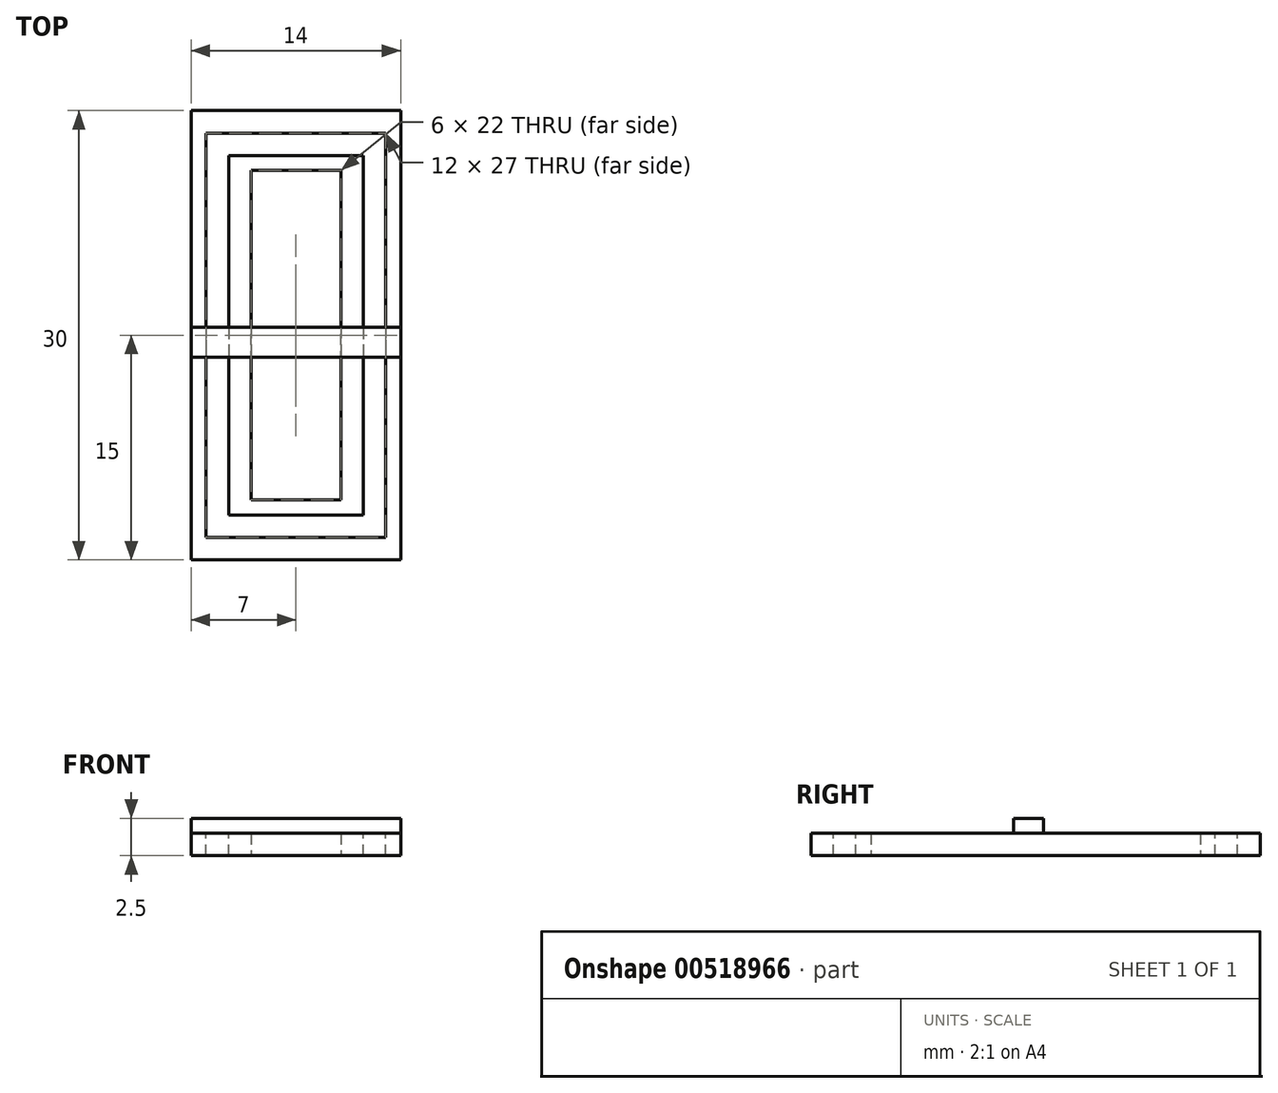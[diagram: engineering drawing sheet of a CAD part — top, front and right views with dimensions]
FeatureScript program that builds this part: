
annotation { "Feature Type Name" : "Feature", "Feature Type Description" : "" }
export const myFeature = defineFeature(function(context is Context, id is Id, definition is map)
    precondition{}
    {
        {
            var Q0;
            Q0=qCreatedBy(makeId("Top.planeOp"),FACE);
            var sketch = newSketch(context, id + "F0", { "sketchPlane" : qUnion([Q0])});
            skLineSegment(sketch, "E0.bottom", {"start": v(-3, 11) * mm, "end": v(3, 11) * mm});
            skLineSegment(sketch, "E0.top", {"start": v(-3, -11) * mm, "end": v(3, -11) * mm});
            skLineSegment(sketch, "E0.left", {"start": v(-3, 11) * mm, "end": v(-3, -11) * mm});
            skLineSegment(sketch, "E0.right", {"start": v(3, 11) * mm, "end": v(3, -11) * mm});
            skLineSegment(sketch, "E1.bottom", {"start": v(-7, 15) * mm, "end": v(7, 15) * mm});
            skLineSegment(sketch, "E1.top", {"start": v(-7, -15) * mm, "end": v(7, -15) * mm});
            skLineSegment(sketch, "E1.left", {"start": v(-7, 15) * mm, "end": v(-7, -15) * mm});
            skLineSegment(sketch, "E1.right", {"start": v(7, 15) * mm, "end": v(7, -15) * mm});
            skLineSegment(sketch, "E2", {"start": v(-3.5, 15) * mm, "end": v(-3.5, 11) * mm, "construction": true});
            skLineSegment(sketch, "E3", {"start": v(3, 0) * mm, "end": v(7, 0) * mm, "construction": true});
            skPoint(sketch, "E3.startSnap0", {"position": v(7, 0) * mm});
            skLineSegment(sketch, "E4", {"start": v(-3, -8.4) * mm, "end": v(-7, -8.4) * mm, "construction": true});
            skLineSegment(sketch, "E5", {"start": v(-2.31, -11) * mm, "end": v(-2.31, -15) * mm, "construction": true});
            skCircle(sketch, "E6", {"center": v(0, 0) * mm, "radius": 2.25 * mm});
            skLineSegment(sketch, "E7", {"start": v(0, 0) * mm, "end": v(0, -11) * mm, "construction": true});
            skLineSegment(sketch, "E8", {"start": v(0, 0) * mm, "end": v(3, 0) * mm, "construction": true});
            skSolve(sketch);
        }
        {
            var Q0;
            Q0=makeQuery(id+"F0.imprint","IMPRINT",FACE,{"disambiguationData":[TD([[makeQuery(id+"F0.imprint","IMPRINT",EDGE,{"derivedFrom":sQuery(id+"F0.wireOp",EDGE,"E0.bottom")}),1.0]])]});
            var Q1;
            Q1=makeQuery(id+"F0.imprint","IMPRINT",FACE,{"disambiguationData":[TD([[makeQuery(id+"F0.imprint","IMPRINT",EDGE,{"derivedFrom":sQuery(id+"F0.wireOp",EDGE,"E0.bottom")}),-1.0]])]});
            extrude(context, id + "F1", {"entities" : qUnion([Q0, Q1]), "oppositeDirection" : true, "depth" : 2.5 * mm, "offsetDistance" : 25 * mm});
        }
        {
            var Q0;
            Q0=makeQuery(id+"F0.imprint","IMPRINT",FACE,{"disambiguationData":[TD([[makeQuery(id+"F0.imprint","IMPRINT",EDGE,{"derivedFrom":sQuery(id+"F0.wireOp",EDGE,"E0.bottom")}),1.0]])]});
            extrude(context, id + "F2", {"entities" : qUnion([Q0]), "operationType" : NewBodyOperationType.ADD, "depth" : 5 * mm, "offsetDistance" : 25 * mm});
        }
        {
            var Q0;
            Q0=makeQuery(id+"F2.opExtrude","CAP_FACE",FACE,{"disambiguationData":[OSD([sQuery(id+"F0.wireOp",EDGE,"E0.bottom"),sQuery(id+"F0.wireOp",EDGE,"E0.top"),sQuery(id+"F0.wireOp",EDGE,"E0.left"),sQuery(id+"F0.wireOp",EDGE,"E0.right"),sQuery(id+"F0.wireOp",EDGE,"E1.bottom"),sQuery(id+"F0.wireOp",EDGE,"E1.top"),sQuery(id+"F0.wireOp",EDGE,"E1.left"),sQuery(id+"F0.wireOp",EDGE,"E1.right")])],"isStart":false});
            var sketch = newSketch(context, id + "F3", { "sketchPlane" : qUnion([Q0])});
            skLineSegment(sketch, "E9.bottom", {"start": v(-6, 13.5) * mm, "end": v(6, 13.5) * mm});
            skLineSegment(sketch, "E9.top", {"start": v(-6, -13.5) * mm, "end": v(6, -13.5) * mm});
            skLineSegment(sketch, "E9.left", {"start": v(-6, 13.5) * mm, "end": v(-6, -13.5) * mm});
            skLineSegment(sketch, "E9.right", {"start": v(6, 13.5) * mm, "end": v(6, -13.5) * mm});
            skLineSegment(sketch, "E10.bottom", {"start": v(-4.5, 12) * mm, "end": v(4.5, 12) * mm});
            skLineSegment(sketch, "E10.top", {"start": v(-4.5, -12) * mm, "end": v(4.5, -12) * mm});
            skLineSegment(sketch, "E10.left", {"start": v(-4.5, 12) * mm, "end": v(-4.5, -12) * mm});
            skLineSegment(sketch, "E10.right", {"start": v(4.5, 12) * mm, "end": v(4.5, -12) * mm});
            skLineSegment(sketch, "E11", {"start": v(4.5, -3.55) * mm, "end": v(6, -3.55) * mm, "construction": true});
            skLineSegment(sketch, "E12", {"start": v(-4.5, -4.54) * mm, "end": v(-6, -4.54) * mm, "construction": true});
            skLineSegment(sketch, "E13", {"start": v(0, -12) * mm, "end": v(0, -13.5) * mm, "construction": true});
            skSolve(sketch);
        }
        {
            var Q0;
            Q0=makeQuery(id+"F3.imprint","IMPRINT",FACE,{"disambiguationData":[TD([[makeQuery(id+"F3.imprint","IMPRINT",EDGE,{"derivedFrom":sQuery(id+"F3.wireOp",EDGE,"E9.bottom")}),-1.0]])]});
            extrude(context, id + "F4", {"entities" : qUnion([Q0]), "operationType" : NewBodyOperationType.REMOVE, "oppositeDirection" : true, "depth" : 1.5 * mm, "offsetDistance" : 25 * mm});
        }
        {
            var Q0;
            {var subQ0=sQuery(id+"F0.wireOp",EDGE,"E1.top");Q0=makeQuery(id+"F2.boolean.opBoolean","MERGE",FACE,{"derivedFrom":[makeQuery(id+"F1.opExtrude","SWEPT_FACE",FACE,{"disambiguationData":[OSD([subQ0])]}),makeQuery(id+"F2.opExtrude","SWEPT_FACE",FACE,{"disambiguationData":[OSD([subQ0])]})]});}
            var sketch = newSketch(context, id + "F5", { "sketchPlane" : qUnion([Q0])});
            skLineSegment(sketch, "E14.bottom", {"start": v(-7, 3.5) * mm, "end": v(7, 3.5) * mm});
            skLineSegment(sketch, "E14.top", {"start": v(-7, -2.5) * mm, "end": v(7, -2.5) * mm});
            skLineSegment(sketch, "E14.left", {"start": v(-7, 3.5) * mm, "end": v(-7, -2.5) * mm});
            skLineSegment(sketch, "E14.right", {"start": v(7, 3.5) * mm, "end": v(7, -2.5) * mm});
            skSolve(sketch);
        }
        {
            var Q0;
            Q0=makeQuery(id+"F5.imprint","IMPRINT",FACE,{"disambiguationData":[TD([[makeQuery(id+"F5.imprint","IMPRINT",EDGE,{"derivedFrom":sQuery(id+"F5.wireOp",EDGE,"E14.bottom")}),-1.0]])]});
            extrude(context, id + "F6", {"entities" : qUnion([Q0]), "operationType" : NewBodyOperationType.REMOVE, "oppositeDirection" : true, "depth" : 45 * mm, "offsetDistance" : 25 * mm});
        }
        {
            var Q0;
            {var subQ0=sQuery(id+"F0.wireOp",EDGE,"E1.right");var subQ1=sQuery(id+"F0.wireOp",EDGE,"E1.left");var subQ2=sQuery(id+"F0.wireOp",EDGE,"E1.bottom");var subQ3=sQuery(id+"F0.wireOp",EDGE,"E1.top");Q0=makeQuery(id+"F4.boolean.opBoolean","SPLIT",FACE,{"disambiguationData":[TD([makeQuery(id+"F1.opExtrude","SWEPT_FACE",FACE,{"disambiguationData":[OSD([subQ2])]})])],"derivedFrom":makeQuery(id+"F2.opExtrude","CAP_FACE",FACE,{"disambiguationData":[OSD([sQuery(id+"F0.wireOp",EDGE,"E0.bottom"),sQuery(id+"F0.wireOp",EDGE,"E0.top"),sQuery(id+"F0.wireOp",EDGE,"E0.left"),sQuery(id+"F0.wireOp",EDGE,"E0.right"),subQ2,subQ3,subQ1,subQ0])],"isStart":false})});}
            var sketch = newSketch(context, id + "F7", { "sketchPlane" : qUnion([Q0])});
            skLineSegment(sketch, "E15.bottom", {"start": v(-7, 0.54) * mm, "end": v(7, 0.54) * mm});
            skLineSegment(sketch, "E15.top", {"start": v(-7, -1.46) * mm, "end": v(7, -1.46) * mm});
            skLineSegment(sketch, "E15.left", {"start": v(-7, 0.54) * mm, "end": v(-7, -1.46) * mm});
            skLineSegment(sketch, "E15.right", {"start": v(7, 0.54) * mm, "end": v(7, -1.46) * mm});
            skSolve(sketch);
        }
        {
            var Q0;
            Q0 = qSketchRegion(id + "F7", true);
            extrude(context, id + "F8", {"entities" : qUnion([Q0]), "depth" : 1 * mm, "offsetDistance" : 25 * mm});
        }
    });
